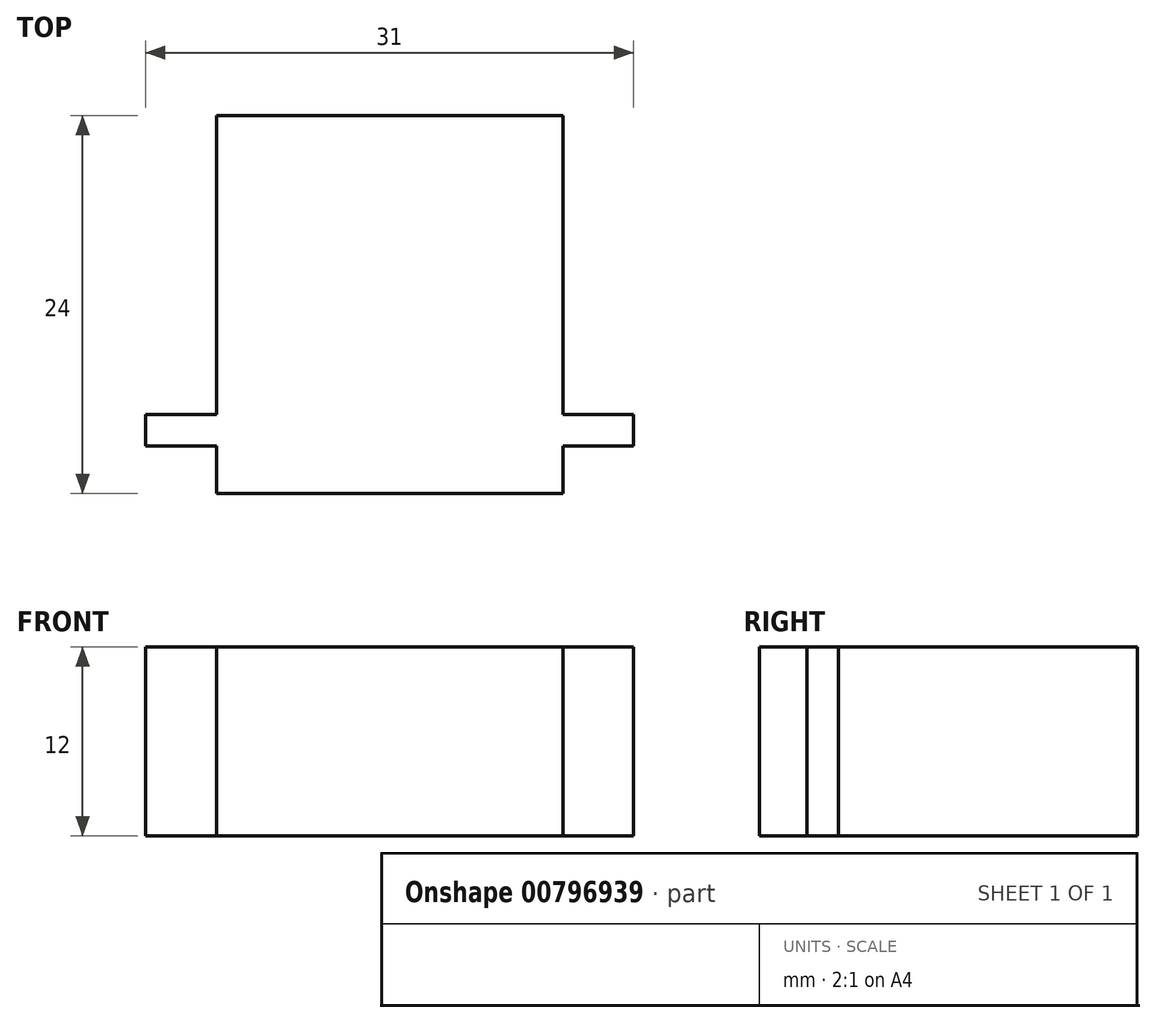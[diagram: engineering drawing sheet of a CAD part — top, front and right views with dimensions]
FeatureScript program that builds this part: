
annotation { "Feature Type Name" : "Feature", "Feature Type Description" : "" }
export const myFeature = defineFeature(function(context is Context, id is Id, definition is map)
    precondition{}
    {
        {
            var Q0;
            Q0=qCreatedBy(makeId("Top.planeOp"),FACE);
            var sketch = newSketch(context, id + "F0", { "sketchPlane" : qUnion([Q0])});
            skLineSegment(sketch, "E0.bottom", {"start": v(11, -12) * mm, "end": v(-11, -12) * mm});
            skLineSegment(sketch, "E0.top", {"start": v(11, 12) * mm, "end": v(-11, 12) * mm});
            skPoint(sketch, "E0.middle", {"position": v(0, 0) * mm});
            skLineSegment(sketch, "E1", {"start": v(11, 12) * mm, "end": v(11, -7) * mm});
            skLineSegment(sketch, "E2", {"start": v(11, -7) * mm, "end": v(15.5, -7) * mm});
            skLineSegment(sketch, "E3", {"start": v(-11, 12) * mm, "end": v(-11, -7) * mm});
            skLineSegment(sketch, "E4", {"start": v(-11, -7) * mm, "end": v(-15.5, -7) * mm});
            skLineSegment(sketch, "E5", {"start": v(-11, -12) * mm, "end": v(-11, -9) * mm});
            skLineSegment(sketch, "E6", {"start": v(-11, -9) * mm, "end": v(-15.5, -9) * mm});
            skLineSegment(sketch, "E7", {"start": v(-15.5, -9) * mm, "end": v(-15.5, -7) * mm});
            skLineSegment(sketch, "E8", {"start": v(11, -12) * mm, "end": v(11, -9) * mm});
            skLineSegment(sketch, "E9", {"start": v(11, -9) * mm, "end": v(15.5, -9) * mm});
            skLineSegment(sketch, "E10", {"start": v(15.5, -9) * mm, "end": v(15.5, -7) * mm});
            skSolve(sketch);
        }
        {
            var Q0;
            Q0 = qSketchRegion(id + "F0", true);
            extrude(context, id + "F1", {"entities" : qUnion([Q0]), "depth" : 12 * mm, "offsetDistance" : 25 * mm});
        }
    });
